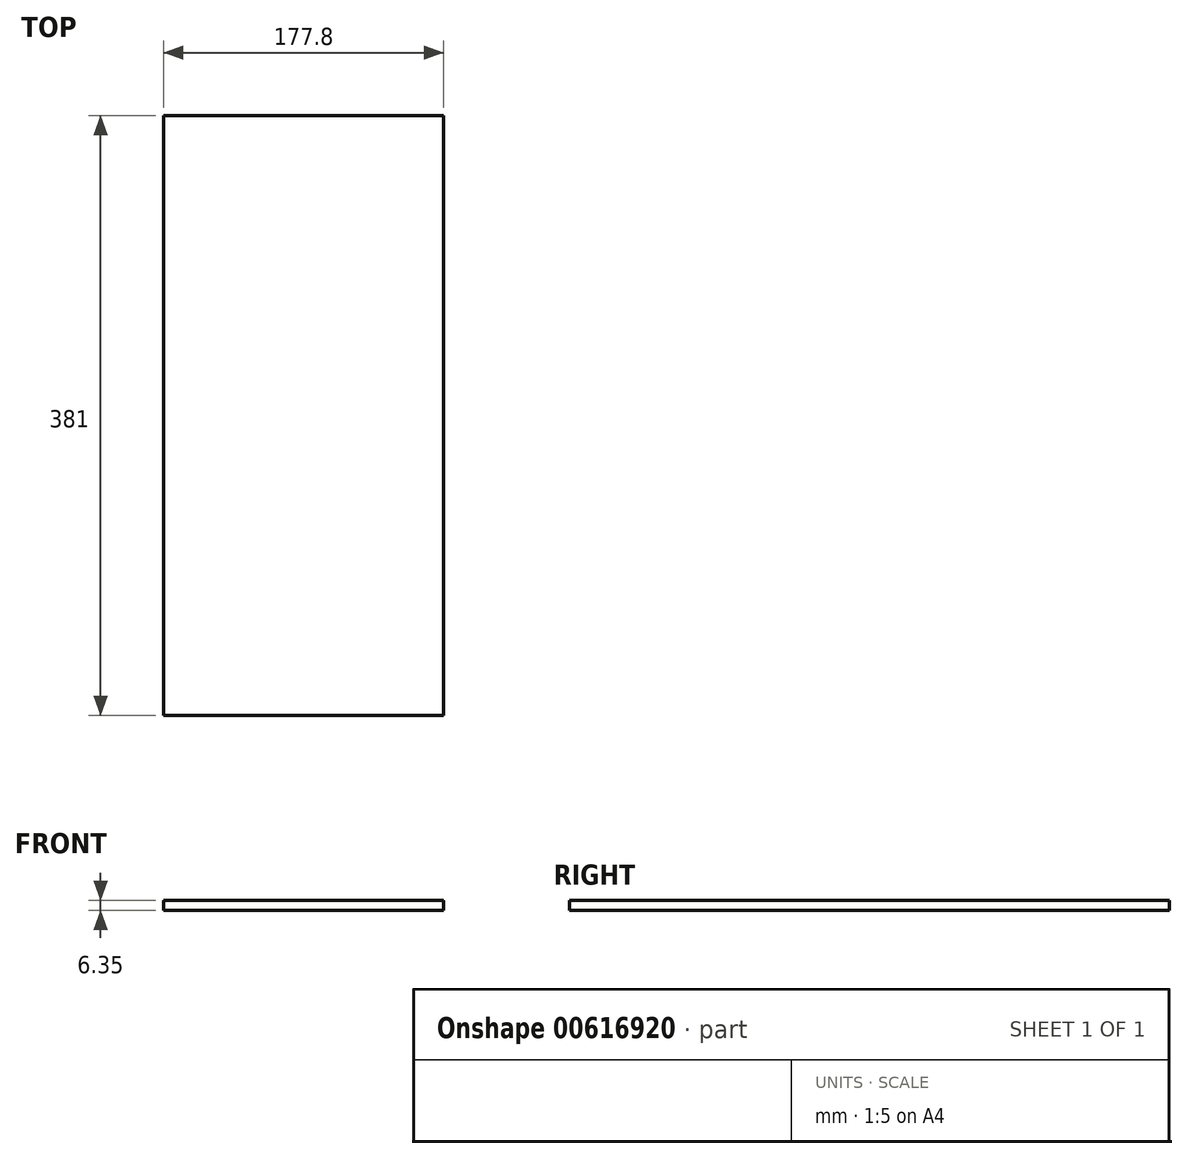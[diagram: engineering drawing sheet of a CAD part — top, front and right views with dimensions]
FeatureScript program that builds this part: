
annotation { "Feature Type Name" : "Feature", "Feature Type Description" : "" }
export const myFeature = defineFeature(function(context is Context, id is Id, definition is map)
    precondition{}
    {
        {
            var Q0;
            Q0=qCreatedBy(makeId("Top.planeOp"),FACE);
            var sketch = newSketch(context, id + "F0", { "sketchPlane" : qUnion([Q0])});
            skLineSegment(sketch, "E0.bottom", {"start": v(-88.9, 190.5) * mm, "end": v(88.9, 190.5) * mm});
            skLineSegment(sketch, "E0.top", {"start": v(-88.9, -190.5) * mm, "end": v(88.9, -190.5) * mm});
            skLineSegment(sketch, "E0.left", {"start": v(-88.9, 190.5) * mm, "end": v(-88.9, -190.5) * mm});
            skLineSegment(sketch, "E0.right", {"start": v(88.9, 190.5) * mm, "end": v(88.9, -190.5) * mm});
            skPoint(sketch, "E0.middle", {"position": v(0, 0) * mm});
            skSolve(sketch);
        }
        {
            var Q0;
            Q0=makeQuery(id+"F0.imprint","IMPRINT",FACE,{"disambiguationData":[TD([[makeQuery(id+"F0.imprint","IMPRINT",EDGE,{"derivedFrom":sQuery(id+"F0.wireOp",EDGE,"E0.bottom")}),-1.0]])]});
            extrude(context, id + "F1", {"entities" : qUnion([Q0]), "depth" : 6.35 * mm, "offsetDistance" : 25.4 * mm});
        }
    });
